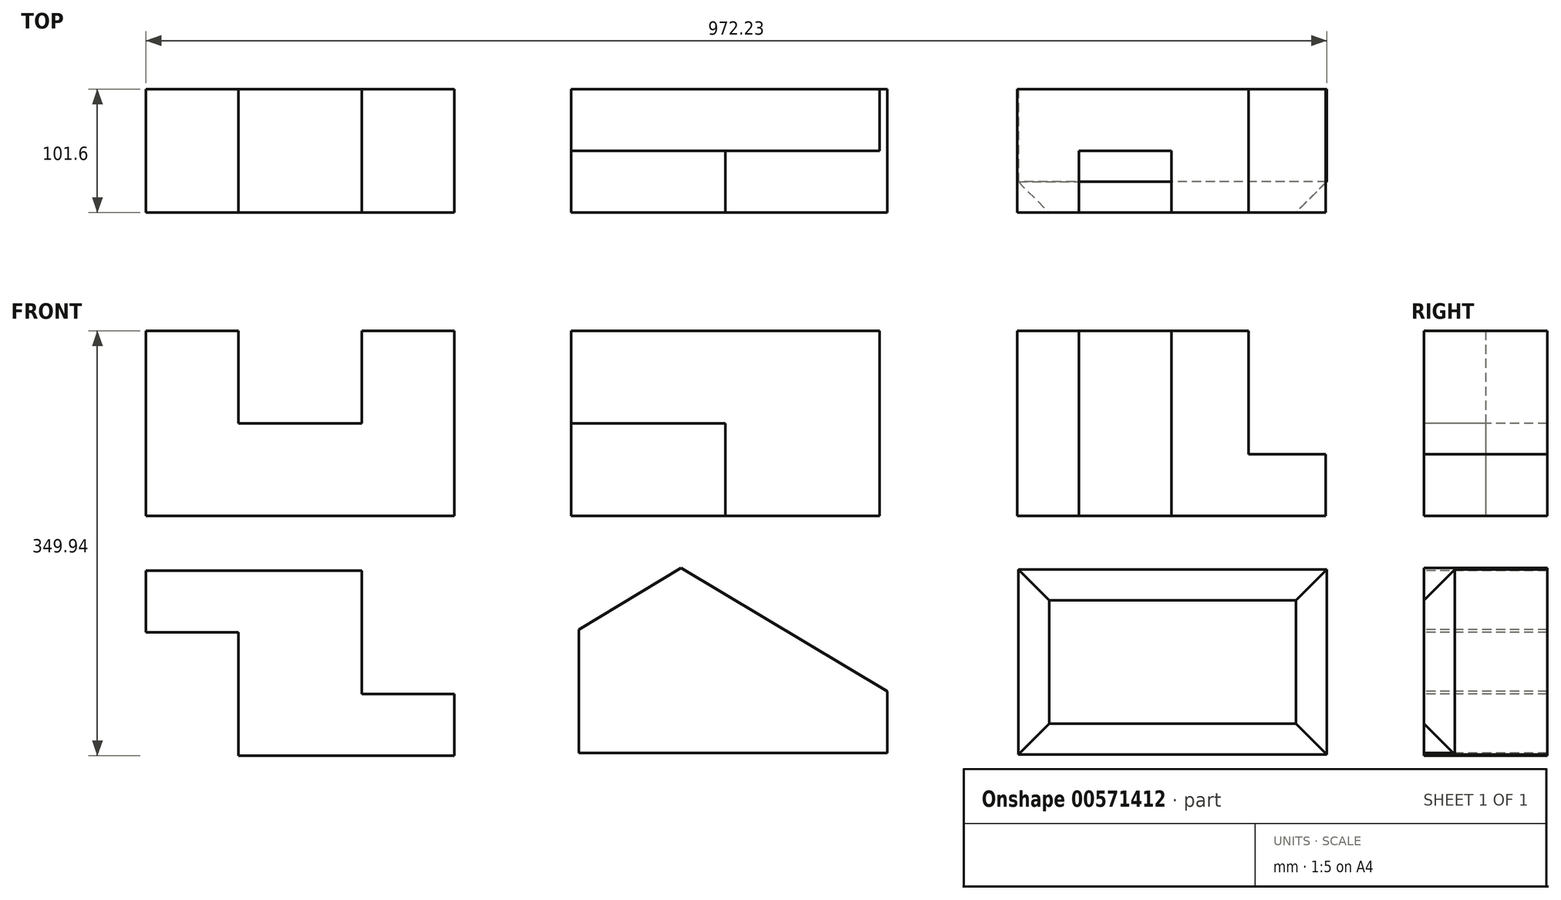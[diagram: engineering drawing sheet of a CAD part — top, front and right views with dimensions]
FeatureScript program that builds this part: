
annotation { "Feature Type Name" : "Feature", "Feature Type Description" : "" }
export const myFeature = defineFeature(function(context is Context, id is Id, definition is map)
    precondition{}
    {
        {
            var Q0;
            Q0=qCreatedBy(makeId("Front.planeOp"),FACE);
            var sketch = newSketch(context, id + "F0", { "sketchPlane" : qUnion([Q0])});
            skLineSegment(sketch, "E0", {"start": v(0, 0) * mm, "end": v(254, 0) * mm});
            skLineSegment(sketch, "E1", {"start": v(254, 0) * mm, "end": v(254, 152.4) * mm});
            skLineSegment(sketch, "E2", {"start": v(254, 152.4) * mm, "end": v(177.8, 152.4) * mm});
            skLineSegment(sketch, "E3", {"start": v(177.8, 152.4) * mm, "end": v(177.8, 76.2) * mm});
            skLineSegment(sketch, "E4", {"start": v(177.8, 76.2) * mm, "end": v(76.2, 76.2) * mm});
            skLineSegment(sketch, "E5", {"start": v(76.2, 76.2) * mm, "end": v(76.2, 152.4) * mm});
            skLineSegment(sketch, "E6", {"start": v(76.2, 152.4) * mm, "end": v(0, 152.4) * mm});
            skLineSegment(sketch, "E7", {"start": v(0, 152.4) * mm, "end": v(0, 0) * mm});
            skSolve(sketch);
        }
        {
            var Q0;
            Q0=makeQuery(id+"F0.imprint","IMPRINT",FACE,{"disambiguationData":[TD([[makeQuery(id+"F0.imprint","IMPRINT",EDGE,{"derivedFrom":sQuery(id+"F0.wireOp",EDGE,"E0")}),1.0]])]});
            extrude(context, id + "F1", {"entities" : qUnion([Q0]), "oppositeDirection" : true, "depth" : 101.6 * mm, "offsetDistance" : 25.4 * mm});
        }
        {
            var Q0;
            Q0=qCreatedBy(makeId("Top.planeOp"),FACE);
            var sketch = newSketch(context, id + "F2", { "sketchPlane" : qUnion([Q0])});
            skLineSegment(sketch, "E8", {"start": v(349.95, 101.6) * mm, "end": v(349.95, 0) * mm});
            skLineSegment(sketch, "E9", {"start": v(349.95, 0) * mm, "end": v(476.95, 0) * mm});
            skLineSegment(sketch, "E10", {"start": v(476.95, 0) * mm, "end": v(476.95, 50.8) * mm});
            skLineSegment(sketch, "E11", {"start": v(476.95, 50.8) * mm, "end": v(603.95, 50.8) * mm});
            skLineSegment(sketch, "E12", {"start": v(603.95, 50.8) * mm, "end": v(603.95, 101.6) * mm});
            skLineSegment(sketch, "E13", {"start": v(603.95, 101.6) * mm, "end": v(349.95, 101.6) * mm});
            skSolve(sketch);
        }
        {
            var Q0;
            Q0 = qSketchRegion(id + "F2", true);
            extrude(context, id + "F3", {"entities" : qUnion([Q0]), "depth" : 152.4 * mm, "offsetDistance" : 25.4 * mm});
        }
        {
            var Q0;
            Q0=makeQuery(id+"F3.opExtrude","SWEPT_FACE",FACE,{"disambiguationData":[OSD([sQuery(id+"F2.wireOp",EDGE,"E9")])]});
            var sketch = newSketch(context, id + "F4", { "sketchPlane" : qUnion([Q0])});
            skLineSegment(sketch, "E14.bottom", {"start": v(349.95, 152.4) * mm, "end": v(476.95, 152.4) * mm});
            skLineSegment(sketch, "E14.top", {"start": v(349.95, 76.2) * mm, "end": v(476.95, 76.2) * mm});
            skLineSegment(sketch, "E14.left", {"start": v(349.95, 152.4) * mm, "end": v(349.95, 76.2) * mm});
            skLineSegment(sketch, "E14.right", {"start": v(476.95, 152.4) * mm, "end": v(476.95, 76.2) * mm});
            skSolve(sketch);
        }
        {
            var Q0;
            Q0=makeQuery(id+"F4.imprint","IMPRINT",FACE,{"disambiguationData":[TD([[makeQuery(id+"F4.imprint","IMPRINT",EDGE,{"derivedFrom":sQuery(id+"F4.wireOp",EDGE,"E14.bottom")}),-1.0]])]});
            extrude(context, id + "F5", {"entities" : qUnion([Q0]), "operationType" : NewBodyOperationType.ADD, "oppositeDirection" : true, "depth" : 50.8 * mm, "offsetDistance" : 25.4 * mm});
        }
        {
            var Q0;
            Q0 = qSketchRegion(id + "F4", true);
            extrude(context, id + "F6", {"entities" : qUnion([Q0]), "operationType" : NewBodyOperationType.REMOVE, "oppositeDirection" : true, "depth" : 50.8 * mm, "offsetDistance" : 25.4 * mm});
        }
        {
            var Q0;
            Q0=qCreatedBy(makeId("Top.planeOp"),FACE);
            var sketch = newSketch(context, id + "F7", { "sketchPlane" : qUnion([Q0])});
            skLineSegment(sketch, "E15", {"start": v(717.46, 101.6) * mm, "end": v(717.46, 0) * mm});
            skLineSegment(sketch, "E16", {"start": v(717.46, 0) * mm, "end": v(768.26, 0) * mm});
            skLineSegment(sketch, "E17", {"start": v(768.26, 0) * mm, "end": v(768.26, 50.8) * mm});
            skLineSegment(sketch, "E18", {"start": v(768.26, 50.8) * mm, "end": v(844.46, 50.8) * mm});
            skLineSegment(sketch, "E19", {"start": v(844.46, 50.8) * mm, "end": v(844.46, 0) * mm});
            skLineSegment(sketch, "E20", {"start": v(844.46, 0) * mm, "end": v(971.46, 0) * mm});
            skLineSegment(sketch, "E21", {"start": v(971.46, 0) * mm, "end": v(971.46, 101.6) * mm});
            skLineSegment(sketch, "E22", {"start": v(971.46, 101.6) * mm, "end": v(717.46, 101.6) * mm});
            skSolve(sketch);
        }
        {
            var Q0;
            Q0 = qSketchRegion(id + "F7", true);
            extrude(context, id + "F8", {"entities" : qUnion([Q0]), "depth" : 152.4 * mm, "offsetDistance" : 25.4 * mm});
        }
        {
            var Q0;
            Q0=makeQuery(id+"F8.opExtrude","SWEPT_FACE",FACE,{"disambiguationData":[OSD([sQuery(id+"F7.wireOp",EDGE,"E20")])]});
            var sketch = newSketch(context, id + "F9", { "sketchPlane" : qUnion([Q0])});
            skPoint(sketch, "E23.oppositeSnap0", {"position": v(907.96, 0) * mm});
            skPoint(sketch, "E23.oppositeSnap1", {"position": v(844.46, 50.8) * mm});
            skLineSegment(sketch, "E23.bottom", {"start": v(971.46, 152.4) * mm, "end": v(907.96, 152.4) * mm});
            skLineSegment(sketch, "E23.top", {"start": v(971.46, 50.8) * mm, "end": v(907.96, 50.8) * mm});
            skLineSegment(sketch, "E23.left", {"start": v(971.46, 152.4) * mm, "end": v(971.46, 50.8) * mm});
            skLineSegment(sketch, "E23.right", {"start": v(907.96, 152.4) * mm, "end": v(907.96, 50.8) * mm});
            skSolve(sketch);
        }
        {
            var Q0;
            Q0 = qSketchRegion(id + "F9", true);
            extrude(context, id + "F10", {"entities" : qUnion([Q0]), "operationType" : NewBodyOperationType.REMOVE, "oppositeDirection" : true, "depth" : 101.6 * mm, "offsetDistance" : 25.4 * mm});
        }
        {
            var Q0;
            Q0=qCreatedBy(makeId("Front.planeOp"),FACE);
            var sketch = newSketch(context, id + "F11", { "sketchPlane" : qUnion([Q0])});
            skLineSegment(sketch, "E24", {"start": v(0, -45.14) * mm, "end": v(0, -95.94) * mm});
            skLineSegment(sketch, "E25", {"start": v(0, -95.94) * mm, "end": v(76.2, -95.94) * mm});
            skLineSegment(sketch, "E26", {"start": v(76.2, -95.94) * mm, "end": v(76.2, -197.54) * mm});
            skLineSegment(sketch, "E27", {"start": v(76.2, -197.54) * mm, "end": v(254, -197.54) * mm});
            skLineSegment(sketch, "E28", {"start": v(254, -197.54) * mm, "end": v(254, -146.74) * mm});
            skLineSegment(sketch, "E29", {"start": v(254, -146.74) * mm, "end": v(177.8, -146.74) * mm});
            skLineSegment(sketch, "E30", {"start": v(177.8, -146.74) * mm, "end": v(177.8, -45.14) * mm});
            skLineSegment(sketch, "E31", {"start": v(177.8, -45.14) * mm, "end": v(0, -45.14) * mm});
            skSolve(sketch);
        }
        {
            var Q0;
            Q0=makeQuery(id+"F11.imprint","IMPRINT",FACE,{"disambiguationData":[TD([[makeQuery(id+"F11.imprint","IMPRINT",EDGE,{"derivedFrom":sQuery(id+"F11.wireOp",EDGE,"E24")}),1.0]])]});
            extrude(context, id + "F12", {"entities" : qUnion([Q0]), "oppositeDirection" : true, "depth" : 101.6 * mm, "offsetDistance" : 25.4 * mm});
        }
        {
            var Q0;
            Q0=qCreatedBy(makeId("Front.planeOp"),FACE);
            var sketch = newSketch(context, id + "F13", { "sketchPlane" : qUnion([Q0])});
            skLineSegment(sketch, "E32", {"start": v(356.49, -195.2) * mm, "end": v(356.49, -93.6) * mm});
            skLineSegment(sketch, "E33", {"start": v(356.49, -93.6) * mm, "end": v(440.56, -42.8) * mm});
            skLineSegment(sketch, "E34", {"start": v(440.56, -42.8) * mm, "end": v(610.49, -144.4) * mm});
            skLineSegment(sketch, "E35", {"start": v(610.49, -144.4) * mm, "end": v(610.49, -195.2) * mm});
            skLineSegment(sketch, "E36", {"start": v(610.49, -195.2) * mm, "end": v(356.49, -195.2) * mm});
            skSolve(sketch);
        }
        {
            var Q0;
            Q0=makeQuery(id+"F13.imprint","IMPRINT",FACE,{"disambiguationData":[TD([[makeQuery(id+"F13.imprint","IMPRINT",EDGE,{"derivedFrom":sQuery(id+"F13.wireOp",EDGE,"E32")}),-1.0]])]});
            extrude(context, id + "F14", {"entities" : qUnion([Q0]), "oppositeDirection" : true, "depth" : 101.6 * mm, "offsetDistance" : 25.4 * mm});
        }
        {
            var Q0;
            Q0=qCreatedBy(makeId("Front.planeOp"),FACE);
            var sketch = newSketch(context, id + "F15", { "sketchPlane" : qUnion([Q0])});
            skLineSegment(sketch, "E37", {"start": v(972.23, -196.45) * mm, "end": v(972.23, -44.05) * mm});
            skLineSegment(sketch, "E38", {"start": v(972.23, -44.05) * mm, "end": v(718.23, -44.05) * mm});
            skLineSegment(sketch, "E39", {"start": v(718.23, -44.05) * mm, "end": v(718.23, -196.45) * mm});
            skLineSegment(sketch, "E40", {"start": v(718.23, -196.45) * mm, "end": v(972.23, -196.45) * mm});
            skSolve(sketch);
        }
        {
            var Q0;
            Q0=makeQuery(id+"F15.imprint","IMPRINT",FACE,{"disambiguationData":[TD([[makeQuery(id+"F15.imprint","IMPRINT",EDGE,{"derivedFrom":sQuery(id+"F15.wireOp",EDGE,"E37")}),1.0]])]});
            extrude(context, id + "F16", {"entities" : qUnion([Q0]), "oppositeDirection" : true, "depth" : 101.6 * mm, "offsetDistance" : 25.4 * mm});
        }
        {
            var Q0;
            Q0=makeQuery(id+"F16.opExtrude","CAP_FACE",FACE,{"disambiguationData":[OSD([sQuery(id+"F15.wireOp",EDGE,"E37"),sQuery(id+"F15.wireOp",EDGE,"E38"),sQuery(id+"F15.wireOp",EDGE,"E39"),sQuery(id+"F15.wireOp",EDGE,"E40")])],"isStart":true});
            chamfer(context, id + "F17", {"entities" : qUnion([Q0]), "width" : 25.4 * mm, "tangentPropagation" : true});
        }
    });
